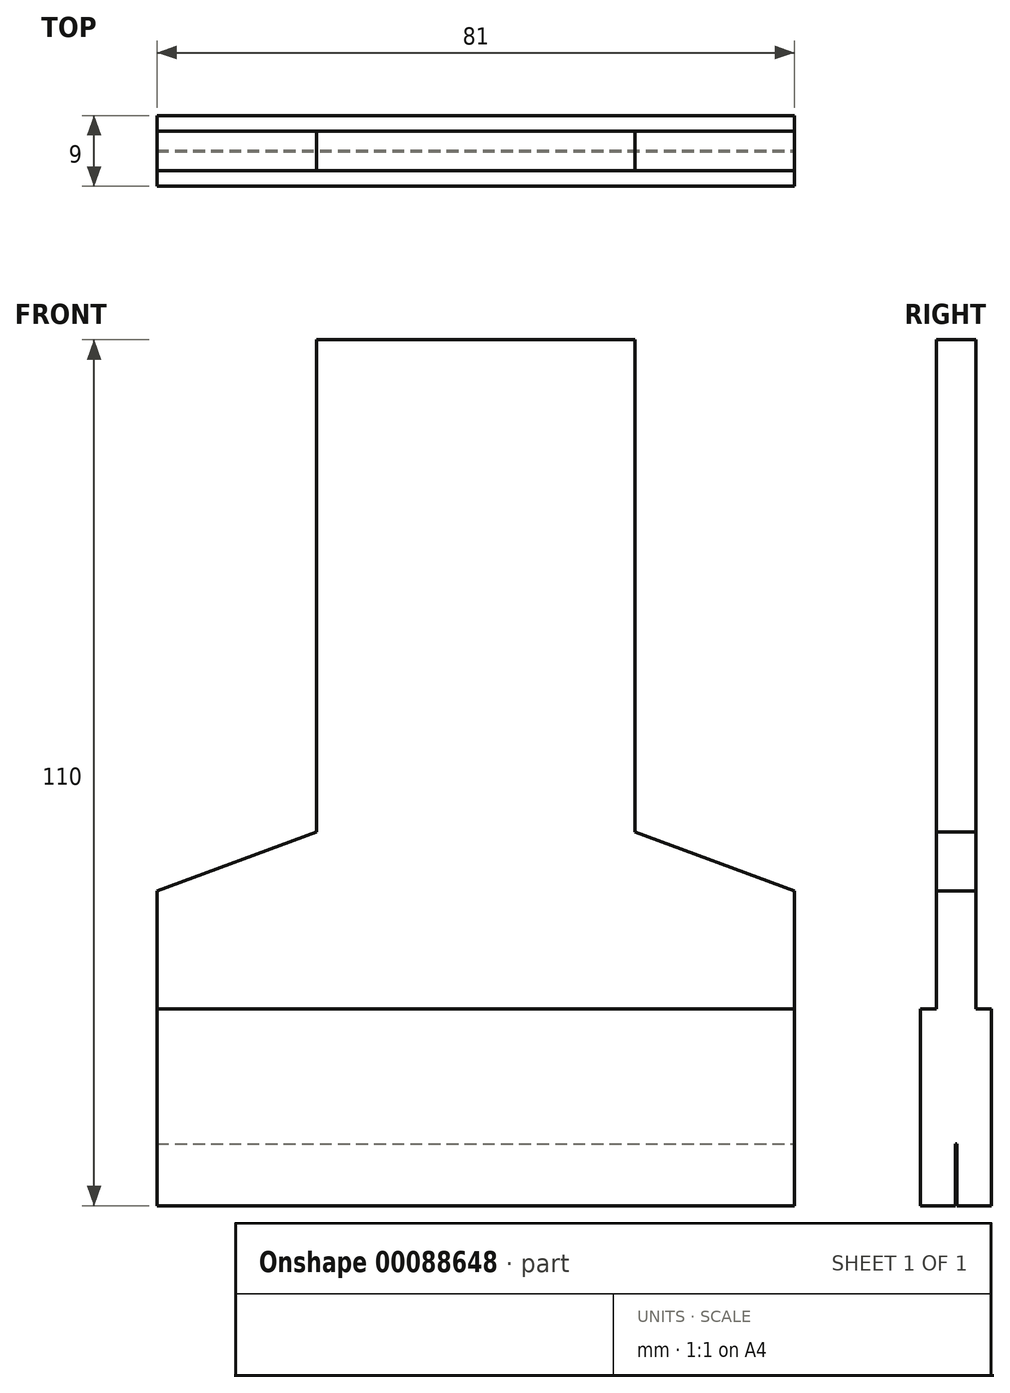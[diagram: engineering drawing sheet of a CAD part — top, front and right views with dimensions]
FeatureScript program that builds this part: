
annotation { "Feature Type Name" : "Feature", "Feature Type Description" : "" }
export const myFeature = defineFeature(function(context is Context, id is Id, definition is map)
    precondition{}
    {
        {
            var Q0;
            Q0=qCreatedBy(makeId("Top.planeOp"),FACE);
            var sketch = newSketch(context, id + "F0", { "sketchPlane" : qUnion([Q0])});
            skLineSegment(sketch, "E0.bottom", {"start": v(0, 0) * mm, "end": v(81, 0) * mm});
            skLineSegment(sketch, "E0.top", {"start": v(0, 9) * mm, "end": v(81, 9) * mm});
            skLineSegment(sketch, "E0.left", {"start": v(0, 0) * mm, "end": v(0, 9) * mm});
            skLineSegment(sketch, "E0.right", {"start": v(81, 0) * mm, "end": v(81, 9) * mm});
            skSolve(sketch);
        }
        {
            var Q0;
            Q0=makeQuery(id+"F0.imprint","IMPRINT",FACE,{"disambiguationData":[TD([[makeQuery(id+"F0.imprint","IMPRINT",EDGE,{"derivedFrom":sQuery(id+"F0.wireOp",EDGE,"E0.bottom")}),1.0]])]});
            extrude(context, id + "F1", {"entities" : qUnion([Q0]), "depth" : 25 * mm});
        }
        {
            var Q0;
            Q0=makeQuery(id+"F1.opExtrude","CAP_FACE",FACE,{"disambiguationData":[OSD([sQuery(id+"F0.wireOp",EDGE,"E0.bottom"),sQuery(id+"F0.wireOp",EDGE,"E0.top"),sQuery(id+"F0.wireOp",EDGE,"E0.left"),sQuery(id+"F0.wireOp",EDGE,"E0.right")])],"isStart":true});
            var sketch = newSketch(context, id + "F2", { "sketchPlane" : qUnion([Q0])});
            skLineSegment(sketch, "E1", {"start": v(0, 0) * mm, "end": v(0, -4.4) * mm});
            skLineSegment(sketch, "E2", {"start": v(0, -9) * mm, "end": v(0, -4.6) * mm});
            skLineSegment(sketch, "E3", {"start": v(0, -4.4) * mm, "end": v(81, -4.4) * mm});
            skLineSegment(sketch, "E4", {"start": v(0, -4.6) * mm, "end": v(81, -4.6) * mm});
            skSolve(sketch);
        }
        {
            var Q0;
            {var subQ0=sQuery(id+"F2.wireOp",EDGE,"E3");Q0=makeQuery(id+"F2.imprint","IMPRINT",FACE,{"disambiguationData":[TD([[makeQuery(id+"F2.imprint","IMPRINT",EDGE,{"derivedFrom":subQ0}),-1.0]])]});}
            extrude(context, id + "F3", {"entities" : qUnion([Q0]), "operationType" : NewBodyOperationType.REMOVE, "oppositeDirection" : true, "depth" : 7.85 * mm});
        }
        {
            var Q0;
            Q0=makeQuery(id+"F1.opExtrude","CAP_FACE",FACE,{"disambiguationData":[OSD([sQuery(id+"F0.wireOp",EDGE,"E0.bottom"),sQuery(id+"F0.wireOp",EDGE,"E0.top"),sQuery(id+"F0.wireOp",EDGE,"E0.left"),sQuery(id+"F0.wireOp",EDGE,"E0.right")])],"isStart":false});
            var sketch = newSketch(context, id + "F4", { "sketchPlane" : qUnion([Q0])});
            skLineSegment(sketch, "E5", {"start": v(0, 4.5) * mm, "end": v(81, 4.5) * mm});
            skLineSegment(sketch, "E6", {"start": v(40.5, 4.5) * mm, "end": v(40.5, 7) * mm});
            skPoint(sketch, "E6.endSnap0", {"position": v(40.5, 9) * mm});
            skLineSegment(sketch, "E7", {"start": v(40.5, 7) * mm, "end": v(40.5, 2) * mm});
            skLineSegment(sketch, "E8", {"start": v(81, 7) * mm, "end": v(0, 7) * mm});
            skLineSegment(sketch, "E9", {"start": v(0, 2) * mm, "end": v(81, 2) * mm});
            skSolve(sketch);
        }
        {
            var Q0;
            {var subQ0=sQuery(id+"F4.wireOp",EDGE,"E5");var subQ1=makeQuery(id+"F1.opExtrude","CAP_EDGE",EDGE,{"disambiguationData":[OSD([sQuery(id+"F0.wireOp",EDGE,"E0.left")])],"isStart":false});var subQ2=makeQuery(id+"F4.imprint","INTERSECT",VERTEX,{"derivedFrom":[subQ1,subQ0]});Q0=makeQuery(id+"F4.imprint","IMPRINT",FACE,{"disambiguationData":[TD([[makeQuery(id+"F4.imprint","IMPRINT",EDGE,{"disambiguationData":[TD([[subQ2,-1.0]])],"derivedFrom":subQ0}),1.0]])]});}
            var Q1;
            {var subQ0=sQuery(id+"F4.wireOp",EDGE,"E5");var subQ1=makeQuery(id+"F1.opExtrude","CAP_EDGE",EDGE,{"disambiguationData":[OSD([sQuery(id+"F0.wireOp",EDGE,"E0.left")])],"isStart":false});var subQ2=makeQuery(id+"F4.imprint","INTERSECT",VERTEX,{"derivedFrom":[subQ1,subQ0]});Q1=makeQuery(id+"F4.imprint","IMPRINT",FACE,{"disambiguationData":[TD([[makeQuery(id+"F4.imprint","IMPRINT",EDGE,{"disambiguationData":[TD([[subQ2,-1.0]])],"derivedFrom":subQ0}),-1.0]])]});}
            var Q2;
            {var subQ0=sQuery(id+"F4.wireOp",EDGE,"E5");var subQ1=makeQuery(id+"F1.opExtrude","CAP_EDGE",EDGE,{"disambiguationData":[OSD([sQuery(id+"F0.wireOp",EDGE,"E0.right")])],"isStart":false});var subQ2=makeQuery(id+"F4.imprint","INTERSECT",VERTEX,{"derivedFrom":[subQ1,subQ0]});Q2=makeQuery(id+"F4.imprint","IMPRINT",FACE,{"disambiguationData":[TD([[makeQuery(id+"F4.imprint","IMPRINT",EDGE,{"disambiguationData":[TD([[subQ2,1.0]])],"derivedFrom":subQ0}),-1.0]])]});}
            var Q3;
            {var subQ0=sQuery(id+"F4.wireOp",EDGE,"E5");var subQ1=makeQuery(id+"F1.opExtrude","CAP_EDGE",EDGE,{"disambiguationData":[OSD([sQuery(id+"F0.wireOp",EDGE,"E0.right")])],"isStart":false});var subQ2=makeQuery(id+"F4.imprint","INTERSECT",VERTEX,{"derivedFrom":[subQ1,subQ0]});Q3=makeQuery(id+"F4.imprint","IMPRINT",FACE,{"disambiguationData":[TD([[makeQuery(id+"F4.imprint","IMPRINT",EDGE,{"disambiguationData":[TD([[subQ2,1.0]])],"derivedFrom":subQ0}),1.0]])]});}
            extrude(context, id + "F5", {"entities" : qUnion([Q0, Q1, Q2, Q3]), "operationType" : NewBodyOperationType.ADD, "depth" : 85 * mm});
        }
        {
            var Q0;
            Q0=makeQuery(id+"F5.opExtrude","SWEPT_FACE",FACE,{"disambiguationData":[OSD([sQuery(id+"F4.wireOp",EDGE,"E9")])]});
            var sketch = newSketch(context, id + "F6", { "sketchPlane" : qUnion([Q0])});
            skLineSegment(sketch, "E10", {"start": v(40.5, 25) * mm, "end": v(40.5, 110) * mm});
            skLineSegment(sketch, "E11", {"start": v(40.5, 25) * mm, "end": v(40.5, 55) * mm});
            skLineSegment(sketch, "E12", {"start": v(40.5, 55) * mm, "end": v(40.5, 40) * mm});
            skLineSegment(sketch, "E13", {"start": v(40.5, 40) * mm, "end": v(81, 40) * mm});
            skLineSegment(sketch, "E14", {"start": v(81, 40) * mm, "end": v(40.5, 55) * mm});
            skLineSegment(sketch, "E15", {"start": v(40.5, 55) * mm, "end": v(0, 40) * mm});
            skLineSegment(sketch, "E16", {"start": v(0, 40) * mm, "end": v(40.5, 40) * mm});
            skLineSegment(sketch, "E17", {"start": v(20.25, 47.5) * mm, "end": v(20.25, 110) * mm});
            skLineSegment(sketch, "E18", {"start": v(60.75, 47.5) * mm, "end": v(60.75, 110) * mm});
            skSolve(sketch);
        }
        {
            var Q0;
            {var subQ4=sQuery(id+"F6.wireOp",EDGE,"E17");Q0=makeQuery(id+"F6.imprint","IMPRINT",FACE,{"disambiguationData":[TD([[makeQuery(id+"F6.imprint","IMPRINT",EDGE,{"derivedFrom":subQ4}),1.0]])]});}
            var Q1;
            {var subQ4=sQuery(id+"F6.wireOp",EDGE,"E18");Q1=makeQuery(id+"F6.imprint","IMPRINT",FACE,{"disambiguationData":[TD([[makeQuery(id+"F6.imprint","IMPRINT",EDGE,{"derivedFrom":subQ4}),-1.0]])]});}
            extrude(context, id + "F7", {"entities" : qUnion([Q0, Q1]), "operationType" : NewBodyOperationType.REMOVE, "oppositeDirection" : true, "depth" : 25 * mm});
        }
    });
